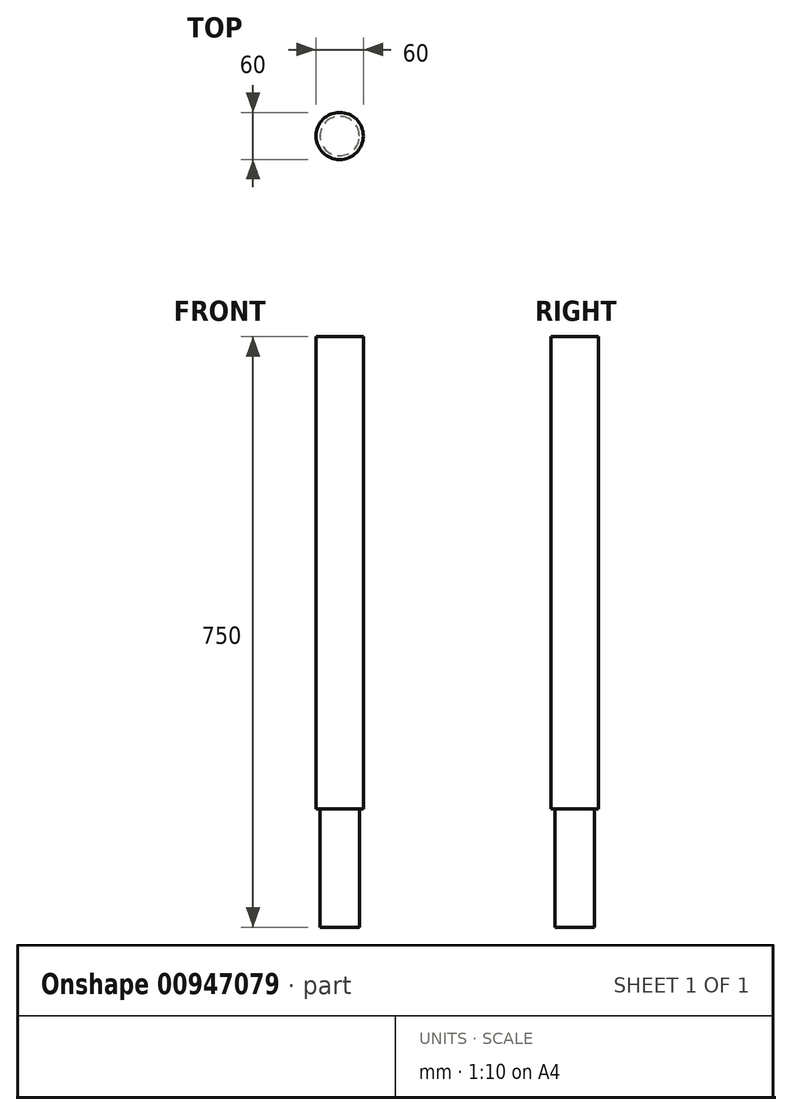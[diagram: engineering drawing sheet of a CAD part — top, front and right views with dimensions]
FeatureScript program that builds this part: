
annotation { "Feature Type Name" : "Feature", "Feature Type Description" : "" }
export const myFeature = defineFeature(function(context is Context, id is Id, definition is map)
    precondition{}
    {
        {
            var Q0;
            Q0=qCreatedBy(makeId("Top.planeOp"),FACE);
            var sketch = newSketch(context, id + "F0", { "sketchPlane" : qUnion([Q0])});
            skCircle(sketch, "E0", {"center": v(0, 0) * mm, "radius": 30 * mm});
            skCircle(sketch, "E1", {"center": v(0, 0) * mm, "radius": 25 * mm});
            skSolve(sketch);
        }
        {
            var Q0;
            Q0=makeQuery(id+"F0.imprint","IMPRINT",FACE,{"disambiguationData":[TD([[makeQuery(id+"F0.imprint","IMPRINT",EDGE,{"derivedFrom":sQuery(id+"F0.wireOp",EDGE,"E1")}),1.0]])]});
            extrude(context, id + "F1", {"entities" : qUnion([Q0]), "depth" : 750 * mm, "offsetDistance" : 25 * mm});
        }
        {
            var Q0;
            Q0 = qSketchRegion(id + "F0", true);
            extrude(context, id + "F2", {"entities" : qUnion([Q0]), "operationType" : NewBodyOperationType.ADD, "depth" : 750 * mm, "offsetDistance" : 25 * mm, "hasSecondDirection" : true, "secondDirectionOppositeDirection" : false, "secondDirectionDepth" : 150 * mm});
        }
    });
